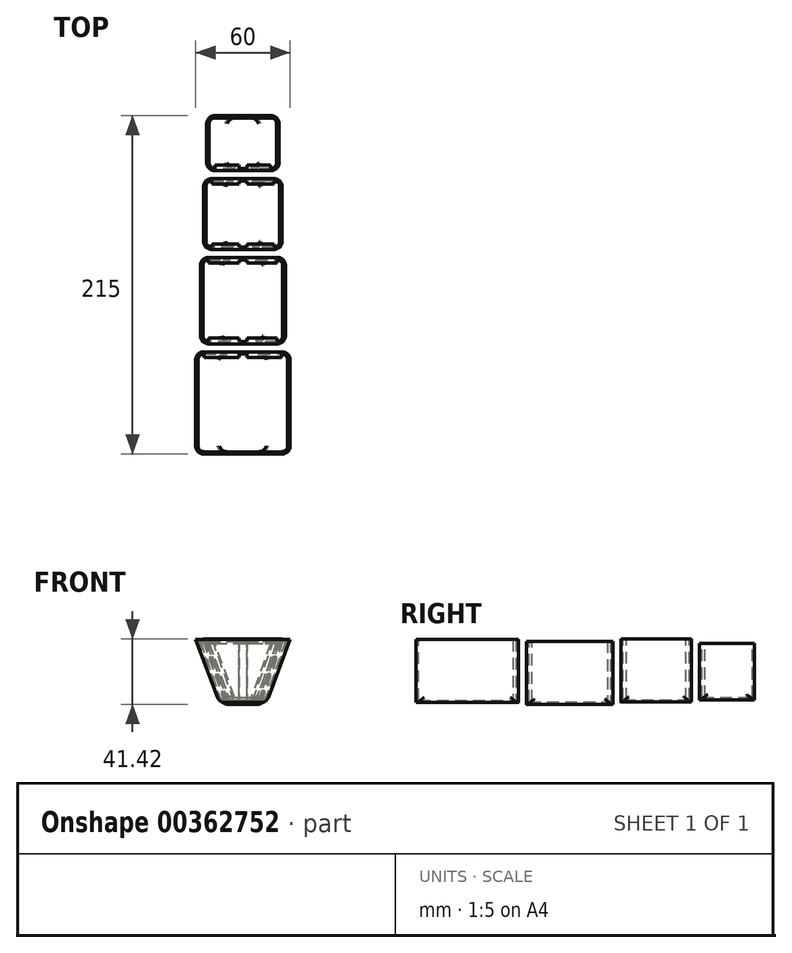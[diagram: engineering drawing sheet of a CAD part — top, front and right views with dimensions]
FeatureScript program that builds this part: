
annotation { "Feature Type Name" : "Feature", "Feature Type Description" : "" }
export const myFeature = defineFeature(function(context is Context, id is Id, definition is map)
    precondition{}
    {
        {
            var Q0;
            Q0=qCreatedBy(makeId("Front.planeOp"),FACE);
            var sketch = newSketch(context, id + "F0", { "sketchPlane" : qUnion([Q0])});
            skLineSegment(sketch, "E0", {"start": v(0, 23.9) * mm, "end": v(-30, 23.9) * mm});
            skLineSegment(sketch, "E1", {"start": v(-30, 23.9) * mm, "end": v(-15, -16.1) * mm});
            skLineSegment(sketch, "E2", {"start": v(-15, -16.1) * mm, "end": v(0, -16.1) * mm});
            skLineSegment(sketch, "E3.MirrorCS", {"start": v(0, 23.9) * mm, "end": v(30, 23.9) * mm});
            skLineSegment(sketch, "E4.MirrorCS", {"start": v(30, 23.9) * mm, "end": v(15, -16.1) * mm});
            skLineSegment(sketch, "E5.MirrorCS", {"start": v(15, -16.1) * mm, "end": v(0, -16.1) * mm});
            skSolve(sketch);
        }
        {
            var Q0;
            Q0=makeQuery(id+"F0.imprint","IMPRINT",FACE,{"disambiguationData":[TD([[makeQuery(id+"F0.imprint","IMPRINT",EDGE,{"derivedFrom":sQuery(id+"F0.wireOp",EDGE,"E0")}),1.0]])]});
            extrude(context, id + "F1", {"entities" : qUnion([Q0]), "depth" : 65 * mm});
        }
        {
            var Q0;
            Q0=makeQuery(id+"F1.opExtrude","SWEPT_EDGE",EDGE,{"disambiguationData":[OSD([sQuery(id+"F0.wireOp",EDGE,"E1"),sQuery(id+"F0.wireOp",EDGE,"E2")])]});
            var Q1;
            Q1=makeQuery(id+"F1.opExtrude","SWEPT_EDGE",EDGE,{"disambiguationData":[OSD([sQuery(id+"F0.wireOp",EDGE,"E4.MirrorCS"),sQuery(id+"F0.wireOp",EDGE,"E5.MirrorCS")])]});
            var Q2;
            Q2=makeQuery(id+"F1.opExtrude","CAP_EDGE",EDGE,{"disambiguationData":[OSD([sQuery(id+"F0.wireOp",EDGE,"E1")])],"isStart":false});
            var Q3;
            Q3=makeQuery(id+"F1.opExtrude","CAP_EDGE",EDGE,{"disambiguationData":[OSD([sQuery(id+"F0.wireOp",EDGE,"E4.MirrorCS")])],"isStart":false});
            var Q4;
            Q4=makeQuery(id+"F1.opExtrude","CAP_EDGE",EDGE,{"disambiguationData":[OSD([sQuery(id+"F0.wireOp",EDGE,"E4.MirrorCS")])],"isStart":true});
            var Q5;
            Q5=makeQuery(id+"F1.opExtrude","CAP_EDGE",EDGE,{"disambiguationData":[OSD([sQuery(id+"F0.wireOp",EDGE,"E1")])],"isStart":true});
            fillet(context, id + "F2", {"entities" : qUnion([Q0, Q1, Q2, Q3, Q4, Q5]), "radius" : 5 * mm, "tangentPropagation" : true, "allowEdgeOverflow" : false});
        }
        {
            var Q0;
            Q0=qCreatedBy(makeId("Front.planeOp"),FACE);
            cPlane(context, id + "F3", {"entities" : qUnion([Q0]), "cplaneType" : CPlaneType.OFFSET, "offset" : 60 * mm, "oppositeDirection" : true, "width" : 150 * mm, "height" : 150 * mm});
        }
        {
            var Q0;
            Q0=qCreatedBy(id+"F3.planeOp",FACE);
            var sketch = newSketch(context, id + "F4", { "sketchPlane" : qUnion([Q0])});
            skLineSegment(sketch, "E6", {"start": v(0, 22.82) * mm, "end": v(27, 22.82) * mm});
            skLineSegment(sketch, "E7", {"start": v(27, 22.82) * mm, "end": v(13, -17.18) * mm});
            skLineSegment(sketch, "E8", {"start": v(13, -17.18) * mm, "end": v(0, -17.18) * mm});
            skLineSegment(sketch, "E9.MirrorCS", {"start": v(0, 22.82) * mm, "end": v(-27, 22.82) * mm});
            skLineSegment(sketch, "E10.MirrorCS", {"start": v(-27, 22.82) * mm, "end": v(-13, -17.18) * mm});
            skLineSegment(sketch, "E11.MirrorCS", {"start": v(-13, -17.18) * mm, "end": v(0, -17.18) * mm});
            skSolve(sketch);
        }
        {
            var Q0;
            Q0=makeQuery(id+"F4.imprint","IMPRINT",FACE,{"disambiguationData":[TD([[makeQuery(id+"F4.imprint","IMPRINT",EDGE,{"derivedFrom":sQuery(id+"F4.wireOp",EDGE,"E6")}),-1.0]])]});
            extrude(context, id + "F5", {"entities" : qUnion([Q0]), "depth" : 55 * mm});
        }
        {
            var Q0;
            Q0=makeQuery(id+"F5.opExtrude","CAP_EDGE",EDGE,{"disambiguationData":[OSD([sQuery(id+"F4.wireOp",EDGE,"E7")])],"isStart":true});
            var Q1;
            Q1=makeQuery(id+"F5.opExtrude","CAP_EDGE",EDGE,{"disambiguationData":[OSD([sQuery(id+"F4.wireOp",EDGE,"E10.MirrorCS")])],"isStart":true});
            var Q2;
            Q2=makeQuery(id+"F5.opExtrude","SWEPT_EDGE",EDGE,{"disambiguationData":[OSD([sQuery(id+"F4.wireOp",EDGE,"E7"),sQuery(id+"F4.wireOp",EDGE,"E8")])]});
            var Q3;
            Q3=makeQuery(id+"F5.opExtrude","SWEPT_EDGE",EDGE,{"disambiguationData":[OSD([sQuery(id+"F4.wireOp",EDGE,"E10.MirrorCS"),sQuery(id+"F4.wireOp",EDGE,"E11.MirrorCS")])]});
            var Q4;
            Q4=makeQuery(id+"F5.opExtrude","CAP_EDGE",EDGE,{"disambiguationData":[OSD([sQuery(id+"F4.wireOp",EDGE,"E10.MirrorCS")])],"isStart":false});
            var Q5;
            Q5=makeQuery(id+"F5.opExtrude","CAP_EDGE",EDGE,{"disambiguationData":[OSD([sQuery(id+"F4.wireOp",EDGE,"E7")])],"isStart":false});
            fillet(context, id + "F6", {"entities" : qUnion([Q0, Q1, Q2, Q3, Q4, Q5]), "radius" : 5 * mm, "tangentPropagation" : true, "allowEdgeOverflow" : false});
        }
        {
            var Q0;
            Q0=qCreatedBy(id+"F3.planeOp",FACE);
            cPlane(context, id + "F7", {"entities" : qUnion([Q0]), "cplaneType" : CPlaneType.OFFSET, "offset" : 50 * mm, "oppositeDirection" : true, "width" : 150 * mm, "height" : 150 * mm});
        }
        {
            var Q0;
            Q0=qCreatedBy(id+"F7.planeOp",FACE);
            var sketch = newSketch(context, id + "F8", { "sketchPlane" : qUnion([Q0])});
            skLineSegment(sketch, "E12", {"start": v(0, 24.24) * mm, "end": v(25, 24.24) * mm});
            skLineSegment(sketch, "E13", {"start": v(25, 24.24) * mm, "end": v(11, -15.76) * mm});
            skLineSegment(sketch, "E14", {"start": v(11, -15.76) * mm, "end": v(0, -15.76) * mm});
            skLineSegment(sketch, "E15.MirrorCS", {"start": v(0, 24.24) * mm, "end": v(-25, 24.24) * mm});
            skLineSegment(sketch, "E16.MirrorCS", {"start": v(-25, 24.24) * mm, "end": v(-11, -15.76) * mm});
            skLineSegment(sketch, "E17.MirrorCS", {"start": v(-11, -15.76) * mm, "end": v(0, -15.76) * mm});
            skSolve(sketch);
        }
        {
            var Q0;
            Q0=makeQuery(id+"F8.imprint","IMPRINT",FACE,{"disambiguationData":[TD([[makeQuery(id+"F8.imprint","IMPRINT",EDGE,{"derivedFrom":sQuery(id+"F8.wireOp",EDGE,"E12")}),-1.0]])]});
            extrude(context, id + "F9", {"entities" : qUnion([Q0]), "depth" : 45 * mm});
        }
        {
            var Q0;
            Q0=makeQuery(id+"F9.opExtrude","CAP_EDGE",EDGE,{"disambiguationData":[OSD([sQuery(id+"F8.wireOp",EDGE,"E13")])],"isStart":true});
            var Q1;
            Q1=makeQuery(id+"F9.opExtrude","CAP_EDGE",EDGE,{"disambiguationData":[OSD([sQuery(id+"F8.wireOp",EDGE,"E16.MirrorCS")])],"isStart":true});
            var Q2;
            Q2=makeQuery(id+"F9.opExtrude","SWEPT_EDGE",EDGE,{"disambiguationData":[OSD([sQuery(id+"F8.wireOp",EDGE,"E13"),sQuery(id+"F8.wireOp",EDGE,"E14")])]});
            var Q3;
            Q3=makeQuery(id+"F9.opExtrude","SWEPT_EDGE",EDGE,{"disambiguationData":[OSD([sQuery(id+"F8.wireOp",EDGE,"E16.MirrorCS"),sQuery(id+"F8.wireOp",EDGE,"E17.MirrorCS")])]});
            var Q4;
            Q4=makeQuery(id+"F9.opExtrude","CAP_EDGE",EDGE,{"disambiguationData":[OSD([sQuery(id+"F8.wireOp",EDGE,"E13")])],"isStart":false});
            var Q5;
            Q5=makeQuery(id+"F9.opExtrude","CAP_EDGE",EDGE,{"disambiguationData":[OSD([sQuery(id+"F8.wireOp",EDGE,"E16.MirrorCS")])],"isStart":false});
            fillet(context, id + "F10", {"entities" : qUnion([Q0, Q1, Q2, Q3, Q4, Q5]), "radius" : 5 * mm, "tangentPropagation" : true, "allowEdgeOverflow" : false});
        }
        {
            var Q0;
            Q0=qCreatedBy(id+"F7.planeOp",FACE);
            cPlane(context, id + "F11", {"entities" : qUnion([Q0]), "cplaneType" : CPlaneType.OFFSET, "offset" : 40 * mm, "oppositeDirection" : true, "width" : 150 * mm, "height" : 150 * mm});
        }
        {
            var Q0;
            Q0=qCreatedBy(id+"F11.planeOp",FACE);
            var sketch = newSketch(context, id + "F12", { "sketchPlane" : qUnion([Q0])});
            skLineSegment(sketch, "E18", {"start": v(0, 21.5) * mm, "end": v(23, 21.5) * mm});
            skLineSegment(sketch, "E19", {"start": v(23, 21.5) * mm, "end": v(10, -14.27) * mm});
            skLineSegment(sketch, "E20", {"start": v(10, -14.27) * mm, "end": v(0, -14.27) * mm});
            skLineSegment(sketch, "E21.MirrorCS", {"start": v(0, 21.5) * mm, "end": v(-23, 21.5) * mm});
            skLineSegment(sketch, "E22.MirrorCS", {"start": v(-23, 21.5) * mm, "end": v(-10, -14.27) * mm});
            skLineSegment(sketch, "E23.MirrorCS", {"start": v(-10, -14.27) * mm, "end": v(0, -14.27) * mm});
            skSolve(sketch);
        }
        {
            var Q0;
            Q0=makeQuery(id+"F12.imprint","IMPRINT",FACE,{"disambiguationData":[TD([[makeQuery(id+"F12.imprint","IMPRINT",EDGE,{"derivedFrom":sQuery(id+"F12.wireOp",EDGE,"E18")}),-1.0]])]});
            extrude(context, id + "F13", {"entities" : qUnion([Q0]), "depth" : 35 * mm});
        }
        {
            var Q0;
            Q0=makeQuery(id+"F13.opExtrude","CAP_EDGE",EDGE,{"disambiguationData":[OSD([sQuery(id+"F12.wireOp",EDGE,"E19")])],"isStart":true});
            var Q1;
            Q1=makeQuery(id+"F13.opExtrude","CAP_EDGE",EDGE,{"disambiguationData":[OSD([sQuery(id+"F12.wireOp",EDGE,"E22.MirrorCS")])],"isStart":true});
            var Q2;
            Q2=makeQuery(id+"F13.opExtrude","SWEPT_EDGE",EDGE,{"disambiguationData":[OSD([sQuery(id+"F12.wireOp",EDGE,"E19"),sQuery(id+"F12.wireOp",EDGE,"E20")])]});
            var Q3;
            Q3=makeQuery(id+"F13.opExtrude","SWEPT_EDGE",EDGE,{"disambiguationData":[OSD([sQuery(id+"F12.wireOp",EDGE,"E22.MirrorCS"),sQuery(id+"F12.wireOp",EDGE,"E23.MirrorCS")])]});
            var Q4;
            Q4=makeQuery(id+"F13.opExtrude","CAP_EDGE",EDGE,{"disambiguationData":[OSD([sQuery(id+"F12.wireOp",EDGE,"E19")])],"isStart":false});
            var Q5;
            Q5=makeQuery(id+"F13.opExtrude","CAP_EDGE",EDGE,{"disambiguationData":[OSD([sQuery(id+"F12.wireOp",EDGE,"E22.MirrorCS")])],"isStart":false});
            fillet(context, id + "F14", {"entities" : qUnion([Q0, Q1, Q2, Q3, Q4, Q5]), "radius" : 5 * mm, "tangentPropagation" : true, "allowEdgeOverflow" : false});
        }
        {
            var Q0;
            Q0=makeQuery(id+"F5.opExtrude","SWEPT_FACE",FACE,{"disambiguationData":[OSD([sQuery(id+"F4.wireOp",EDGE,"E6"),sQuery(id+"F4.wireOp",EDGE,"E9.MirrorCS")])]});
            shell(context, id + "F15", {"entities" : qUnion([Q0]), "thickness" : 1.6 * mm});
        }
        {
            var Q0;
            Q0=makeQuery(id+"F13.opExtrude","SWEPT_FACE",FACE,{"disambiguationData":[OSD([sQuery(id+"F12.wireOp",EDGE,"E18"),sQuery(id+"F12.wireOp",EDGE,"E21.MirrorCS")])]});
            shell(context, id + "F16", {"entities" : qUnion([Q0]), "thickness" : 1.5 * mm});
        }
        {
            var Q0;
            Q0=makeQuery(id+"F1.opExtrude","SWEPT_FACE",FACE,{"disambiguationData":[OSD([sQuery(id+"F0.wireOp",EDGE,"E0"),sQuery(id+"F0.wireOp",EDGE,"E3.MirrorCS")])]});
            shell(context, id + "F17", {"entities" : qUnion([Q0]), "thickness" : 1.5 * mm});
        }
        {
            var Q0;
            Q0=makeQuery(id+"F9.opExtrude","SWEPT_FACE",FACE,{"disambiguationData":[OSD([sQuery(id+"F8.wireOp",EDGE,"E12"),sQuery(id+"F8.wireOp",EDGE,"E15.MirrorCS")])]});
            shell(context, id + "F18", {"entities" : qUnion([Q0]), "thickness" : 1.5 * mm});
        }
        {
            var Q0;
            {var subQ0=sQuery(id+"F8.wireOp",EDGE,"E17.MirrorCS");var subQ1=sQuery(id+"F8.wireOp",EDGE,"E16.MirrorCS");var subQ2=sQuery(id+"F8.wireOp",EDGE,"E15.MirrorCS");var subQ3=sQuery(id+"F8.wireOp",EDGE,"E14");var subQ4=sQuery(id+"F8.wireOp",EDGE,"E13");var subQ5=sQuery(id+"F8.wireOp",EDGE,"E12");Q0=makeQuery(id+"F18.opShell","OFFSET_FACE",FACE,{"disambiguationData":[OSD([subQ5,subQ4,subQ3,subQ2,subQ1,subQ0]),TDD([makeQuery(id+"F9.opExtrude","CAP_FACE",FACE,{"disambiguationData":[OSD([subQ5,subQ4,subQ3,subQ2,subQ1,subQ0])],"isStart":true})])]});}
            var sketch = newSketch(context, id + "F19", { "sketchPlane" : qUnion([Q0])});
            skLineSegment(sketch, "E24", {"start": v(-2.5, -14.26) * mm, "end": v(-2.5, 24.24) * mm});
            skLineSegment(sketch, "E25", {"start": v(-2.5, 24.24) * mm, "end": v(-19.7, 24.24) * mm});
            skLineSegment(sketch, "E26", {"start": v(-19.7, 24.24) * mm, "end": v(-6.23, -14.26) * mm});
            skLineSegment(sketch, "E27", {"start": v(-6.23, -14.26) * mm, "end": v(-2.5, -14.26) * mm});
            skLineSegment(sketch, "E28", {"start": v(0, -14.26) * mm, "end": v(0, 24.24) * mm, "construction": true});
            skLineSegment(sketch, "E29.MirrorCS", {"start": v(2.5, -14.26) * mm, "end": v(2.5, 24.24) * mm});
            skLineSegment(sketch, "E30.MirrorCS", {"start": v(2.5, 24.24) * mm, "end": v(19.7, 24.24) * mm});
            skLineSegment(sketch, "E31.MirrorCS", {"start": v(19.7, 24.24) * mm, "end": v(6.23, -14.26) * mm});
            skLineSegment(sketch, "E32.MirrorCS", {"start": v(6.23, -14.26) * mm, "end": v(2.5, -14.26) * mm});
            skSolve(sketch);
        }
        {
            var Q0;
            Q0=makeQuery(id+"F19.imprint","IMPRINT",FACE,{"disambiguationData":[TD([[makeQuery(id+"F19.imprint","IMPRINT",EDGE,{"derivedFrom":sQuery(id+"F19.wireOp",EDGE,"E29.MirrorCS")}),-1.0]])]});
            var Q1;
            Q1=makeQuery(id+"F19.imprint","IMPRINT",FACE,{"disambiguationData":[TD([[makeQuery(id+"F19.imprint","IMPRINT",EDGE,{"derivedFrom":sQuery(id+"F19.wireOp",EDGE,"E24")}),1.0]])]});
            extrude(context, id + "F20", {"entities" : qUnion([Q0, Q1]), "operationType" : NewBodyOperationType.ADD, "depth" : 2 * mm});
        }
        {
            var Q0;
            {var subQ0=sQuery(id+"F8.wireOp",EDGE,"E17.MirrorCS");var subQ1=sQuery(id+"F8.wireOp",EDGE,"E16.MirrorCS");var subQ2=sQuery(id+"F8.wireOp",EDGE,"E15.MirrorCS");var subQ3=sQuery(id+"F8.wireOp",EDGE,"E14");var subQ4=sQuery(id+"F8.wireOp",EDGE,"E13");var subQ5=sQuery(id+"F8.wireOp",EDGE,"E12");Q0=makeQuery(id+"F18.opShell","OFFSET_FACE",FACE,{"disambiguationData":[OSD([subQ5,subQ4,subQ3,subQ2,subQ1,subQ0]),TDD([makeQuery(id+"F9.opExtrude","CAP_FACE",FACE,{"disambiguationData":[OSD([subQ5,subQ4,subQ3,subQ2,subQ1,subQ0])],"isStart":false})])]});}
            var sketch = newSketch(context, id + "F21", { "sketchPlane" : qUnion([Q0])});
            skLineSegment(sketch, "E33", {"start": v(0, -14.26) * mm, "end": v(0, 24.24) * mm, "construction": true});
            skPoint(sketch, "E34.0", {"position": v(-6.23, -14.26) * mm});
            skPoint(sketch, "E35.0", {"position": v(6.23, -14.26) * mm});
            skPoint(sketch, "E36.0", {"position": v(19.7, 24.24) * mm});
            skPoint(sketch, "E37.0", {"position": v(-19.7, 24.24) * mm});
            skLineSegment(sketch, "E38.0", {"start": v(6.23, -14.26) * mm, "end": v(-6.23, -14.26) * mm});
            skLineSegment(sketch, "E39", {"start": v(-2.5, -14.26) * mm, "end": v(-2.5, 24.24) * mm});
            skLineSegment(sketch, "E40", {"start": v(-2.5, -14.26) * mm, "end": v(-6.23, -14.26) * mm});
            skLineSegment(sketch, "E41", {"start": v(-19.7, 24.24) * mm, "end": v(-2.5, 24.24) * mm});
            skLineSegment(sketch, "E42.MirrorCS", {"start": v(2.5, -14.26) * mm, "end": v(2.5, 24.24) * mm});
            skLineSegment(sketch, "E43.MirrorCS", {"start": v(2.5, -14.26) * mm, "end": v(6.23, -14.26) * mm});
            skLineSegment(sketch, "E44.MirrorCS", {"start": v(19.7, 24.24) * mm, "end": v(2.5, 24.24) * mm});
            skLineSegment(sketch, "E45", {"start": v(-6.23, -14.26) * mm, "end": v(-19.7, 24.24) * mm});
            skLineSegment(sketch, "E46.MirrorCS", {"start": v(6.23, -14.26) * mm, "end": v(19.7, 24.24) * mm});
            skSolve(sketch);
        }
        {
            var Q0;
            Q0=makeQuery(id+"F21.imprint","IMPRINT",FACE,{"disambiguationData":[TD([[makeQuery(id+"F21.imprint","IMPRINT",EDGE,{"derivedFrom":sQuery(id+"F21.wireOp",EDGE,"E39")}),1.0]])]});
            var Q1;
            Q1=makeQuery(id+"F21.imprint","IMPRINT",FACE,{"disambiguationData":[TD([[makeQuery(id+"F21.imprint","IMPRINT",EDGE,{"derivedFrom":sQuery(id+"F21.wireOp",EDGE,"E42.MirrorCS")}),-1.0]])]});
            extrude(context, id + "F22", {"entities" : qUnion([Q0, Q1]), "operationType" : NewBodyOperationType.ADD, "depth" : 2 * mm});
        }
        {
            var Q0;
            {var subQ0=sQuery(id+"F12.wireOp",EDGE,"E23.MirrorCS");var subQ1=sQuery(id+"F12.wireOp",EDGE,"E22.MirrorCS");var subQ2=sQuery(id+"F12.wireOp",EDGE,"E21.MirrorCS");var subQ3=sQuery(id+"F12.wireOp",EDGE,"E20");var subQ4=sQuery(id+"F12.wireOp",EDGE,"E19");var subQ5=sQuery(id+"F12.wireOp",EDGE,"E18");Q0=makeQuery(id+"F16.opShell","OFFSET_FACE",FACE,{"disambiguationData":[OSD([subQ5,subQ4,subQ3,subQ2,subQ1,subQ0]),TDD([makeQuery(id+"F13.opExtrude","CAP_FACE",FACE,{"disambiguationData":[OSD([subQ5,subQ4,subQ3,subQ2,subQ1,subQ0])],"isStart":false})])]});}
            var sketch = newSketch(context, id + "F23", { "sketchPlane" : qUnion([Q0])});
            skLineSegment(sketch, "E47", {"start": v(0, -12.77) * mm, "end": v(0, 21.5) * mm, "construction": true});
            skLineSegment(sketch, "E48", {"start": v(-2.5, -12.77) * mm, "end": v(-2.5, 21.5) * mm});
            skLineSegment(sketch, "E49", {"start": v(-2.5, -12.77) * mm, "end": v(-5.23, -12.77) * mm});
            skLineSegment(sketch, "E50", {"start": v(-5.23, -12.77) * mm, "end": v(-17.68, 21.5) * mm});
            skLineSegment(sketch, "E51", {"start": v(-17.68, 21.5) * mm, "end": v(-2.5, 21.5) * mm});
            skLineSegment(sketch, "E52.MirrorCS", {"start": v(2.5, -12.77) * mm, "end": v(2.5, 21.5) * mm});
            skLineSegment(sketch, "E53.MirrorCS", {"start": v(2.5, -12.77) * mm, "end": v(5.23, -12.77) * mm});
            skLineSegment(sketch, "E54.MirrorCS", {"start": v(5.23, -12.77) * mm, "end": v(17.68, 21.5) * mm});
            skLineSegment(sketch, "E55.MirrorCS", {"start": v(17.68, 21.5) * mm, "end": v(2.5, 21.5) * mm});
            skSolve(sketch);
        }
        {
            var Q0;
            Q0=qSketchRegion(id+"F23",true);
            extrude(context, id + "F24", {"entities" : qUnion([Q0]), "operationType" : NewBodyOperationType.ADD, "depth" : 2 * mm});
        }
        {
            var Q0;
            {var subQ0=sQuery(id+"F4.wireOp",EDGE,"E11.MirrorCS");var subQ1=sQuery(id+"F4.wireOp",EDGE,"E10.MirrorCS");var subQ2=sQuery(id+"F4.wireOp",EDGE,"E9.MirrorCS");var subQ3=sQuery(id+"F4.wireOp",EDGE,"E8");var subQ4=sQuery(id+"F4.wireOp",EDGE,"E7");var subQ5=sQuery(id+"F4.wireOp",EDGE,"E6");Q0=makeQuery(id+"F15.opShell","OFFSET_FACE",FACE,{"disambiguationData":[OSD([subQ5,subQ4,subQ3,subQ2,subQ1,subQ0]),TDD([makeQuery(id+"F5.opExtrude","CAP_FACE",FACE,{"disambiguationData":[OSD([subQ5,subQ4,subQ3,subQ2,subQ1,subQ0])],"isStart":true})])]});}
            var sketch = newSketch(context, id + "F25", { "sketchPlane" : qUnion([Q0])});
            skLineSegment(sketch, "E56", {"start": v(0, 22.82) * mm, "end": v(0, -15.58) * mm, "construction": true});
            skLineSegment(sketch, "E57", {"start": v(-2.5, 22.82) * mm, "end": v(-2.5, -15.58) * mm});
            skLineSegment(sketch, "E58", {"start": v(-2.5, 22.82) * mm, "end": v(-21.7, 22.82) * mm});
            skLineSegment(sketch, "E59", {"start": v(-21.7, 22.82) * mm, "end": v(-8.26, -15.58) * mm});
            skLineSegment(sketch, "E60", {"start": v(-8.26, -15.58) * mm, "end": v(-2.5, -15.58) * mm});
            skLineSegment(sketch, "E61.MirrorCS", {"start": v(2.5, 22.82) * mm, "end": v(2.5, -15.58) * mm});
            skLineSegment(sketch, "E62.MirrorCS", {"start": v(2.5, 22.82) * mm, "end": v(21.7, 22.82) * mm});
            skLineSegment(sketch, "E63.MirrorCS", {"start": v(21.7, 22.82) * mm, "end": v(8.26, -15.58) * mm});
            skLineSegment(sketch, "E64.MirrorCS", {"start": v(8.26, -15.58) * mm, "end": v(2.5, -15.58) * mm});
            skSolve(sketch);
        }
        {
            var Q0;
            Q0=qSketchRegion(id+"F25",true);
            extrude(context, id + "F26", {"entities" : qUnion([Q0]), "operationType" : NewBodyOperationType.ADD, "depth" : 2 * mm});
        }
        {
            var Q0;
            {var subQ0=sQuery(id+"F4.wireOp",EDGE,"E11.MirrorCS");var subQ1=sQuery(id+"F4.wireOp",EDGE,"E10.MirrorCS");var subQ2=sQuery(id+"F4.wireOp",EDGE,"E9.MirrorCS");var subQ3=sQuery(id+"F4.wireOp",EDGE,"E8");var subQ4=sQuery(id+"F4.wireOp",EDGE,"E7");var subQ5=sQuery(id+"F4.wireOp",EDGE,"E6");Q0=makeQuery(id+"F15.opShell","OFFSET_FACE",FACE,{"disambiguationData":[OSD([subQ5,subQ4,subQ3,subQ2,subQ1,subQ0]),TDD([makeQuery(id+"F5.opExtrude","CAP_FACE",FACE,{"disambiguationData":[OSD([subQ5,subQ4,subQ3,subQ2,subQ1,subQ0])],"isStart":false})])]});}
            var sketch = newSketch(context, id + "F27", { "sketchPlane" : qUnion([Q0])});
            skLineSegment(sketch, "E65", {"start": v(0, -15.58) * mm, "end": v(0, 22.82) * mm, "construction": true});
            skLineSegment(sketch, "E66", {"start": v(-2.5, -15.58) * mm, "end": v(-2.5, 22.82) * mm});
            skLineSegment(sketch, "E67", {"start": v(-2.5, -15.58) * mm, "end": v(-8.26, -15.58) * mm});
            skLineSegment(sketch, "E68", {"start": v(-8.26, -15.58) * mm, "end": v(-21.7, 22.82) * mm});
            skLineSegment(sketch, "E69", {"start": v(-21.7, 22.82) * mm, "end": v(-2.5, 22.82) * mm});
            skLineSegment(sketch, "E70.MirrorCS", {"start": v(2.5, -15.58) * mm, "end": v(2.5, 22.82) * mm});
            skLineSegment(sketch, "E71.MirrorCS", {"start": v(2.5, -15.58) * mm, "end": v(8.26, -15.58) * mm});
            skLineSegment(sketch, "E72.MirrorCS", {"start": v(8.26, -15.58) * mm, "end": v(21.7, 22.82) * mm});
            skLineSegment(sketch, "E73.MirrorCS", {"start": v(21.7, 22.82) * mm, "end": v(2.5, 22.82) * mm});
            skSolve(sketch);
        }
        {
            var Q0;
            Q0=makeQuery(id+"F27.imprint","IMPRINT",FACE,{"disambiguationData":[TD([[makeQuery(id+"F27.imprint","IMPRINT",EDGE,{"derivedFrom":sQuery(id+"F27.wireOp",EDGE,"E70.MirrorCS")}),-1.0]])]});
            var Q1;
            Q1=makeQuery(id+"F27.imprint","IMPRINT",FACE,{"disambiguationData":[TD([[makeQuery(id+"F27.imprint","IMPRINT",EDGE,{"derivedFrom":sQuery(id+"F27.wireOp",EDGE,"E66")}),1.0]])]});
            extrude(context, id + "F28", {"entities" : qUnion([Q0, Q1]), "operationType" : NewBodyOperationType.ADD, "depth" : 2 * mm});
        }
        {
            var Q0;
            {var subQ0=sQuery(id+"F0.wireOp",EDGE,"E5.MirrorCS");var subQ1=sQuery(id+"F0.wireOp",EDGE,"E4.MirrorCS");var subQ2=sQuery(id+"F0.wireOp",EDGE,"E3.MirrorCS");var subQ3=sQuery(id+"F0.wireOp",EDGE,"E2");var subQ4=sQuery(id+"F0.wireOp",EDGE,"E1");var subQ5=sQuery(id+"F0.wireOp",EDGE,"E0");Q0=makeQuery(id+"F17.opShell","OFFSET_FACE",FACE,{"disambiguationData":[OSD([subQ5,subQ4,subQ3,subQ2,subQ1,subQ0]),TDD([makeQuery(id+"F1.opExtrude","CAP_FACE",FACE,{"disambiguationData":[OSD([subQ5,subQ4,subQ3,subQ2,subQ1,subQ0])],"isStart":true})])]});}
            var sketch = newSketch(context, id + "F29", { "sketchPlane" : qUnion([Q0])});
            skLineSegment(sketch, "E74", {"start": v(0, -14.6) * mm, "end": v(0, 23.9) * mm, "construction": true});
            skLineSegment(sketch, "E75", {"start": v(-2.5, 23.9) * mm, "end": v(-2.5, -14.6) * mm});
            skLineSegment(sketch, "E76", {"start": v(-2.5, 23.9) * mm, "end": v(-24.66, 23.9) * mm});
            skLineSegment(sketch, "E77", {"start": v(-24.66, 23.9) * mm, "end": v(-10.22, -14.6) * mm});
            skLineSegment(sketch, "E78", {"start": v(-10.22, -14.6) * mm, "end": v(-2.5, -14.6) * mm});
            skLineSegment(sketch, "E79.MirrorCS", {"start": v(2.5, 23.9) * mm, "end": v(2.5, -14.6) * mm});
            skLineSegment(sketch, "E80.MirrorCS", {"start": v(2.5, 23.9) * mm, "end": v(24.66, 23.9) * mm});
            skLineSegment(sketch, "E81.MirrorCS", {"start": v(24.66, 23.9) * mm, "end": v(10.22, -14.6) * mm});
            skLineSegment(sketch, "E82.MirrorCS", {"start": v(10.22, -14.6) * mm, "end": v(2.5, -14.6) * mm});
            skSolve(sketch);
        }
        {
            var Q0;
            Q0=qSketchRegion(id+"F29",true);
            extrude(context, id + "F30", {"entities" : qUnion([Q0]), "operationType" : NewBodyOperationType.ADD, "depth" : 2 * mm});
        }
    });
